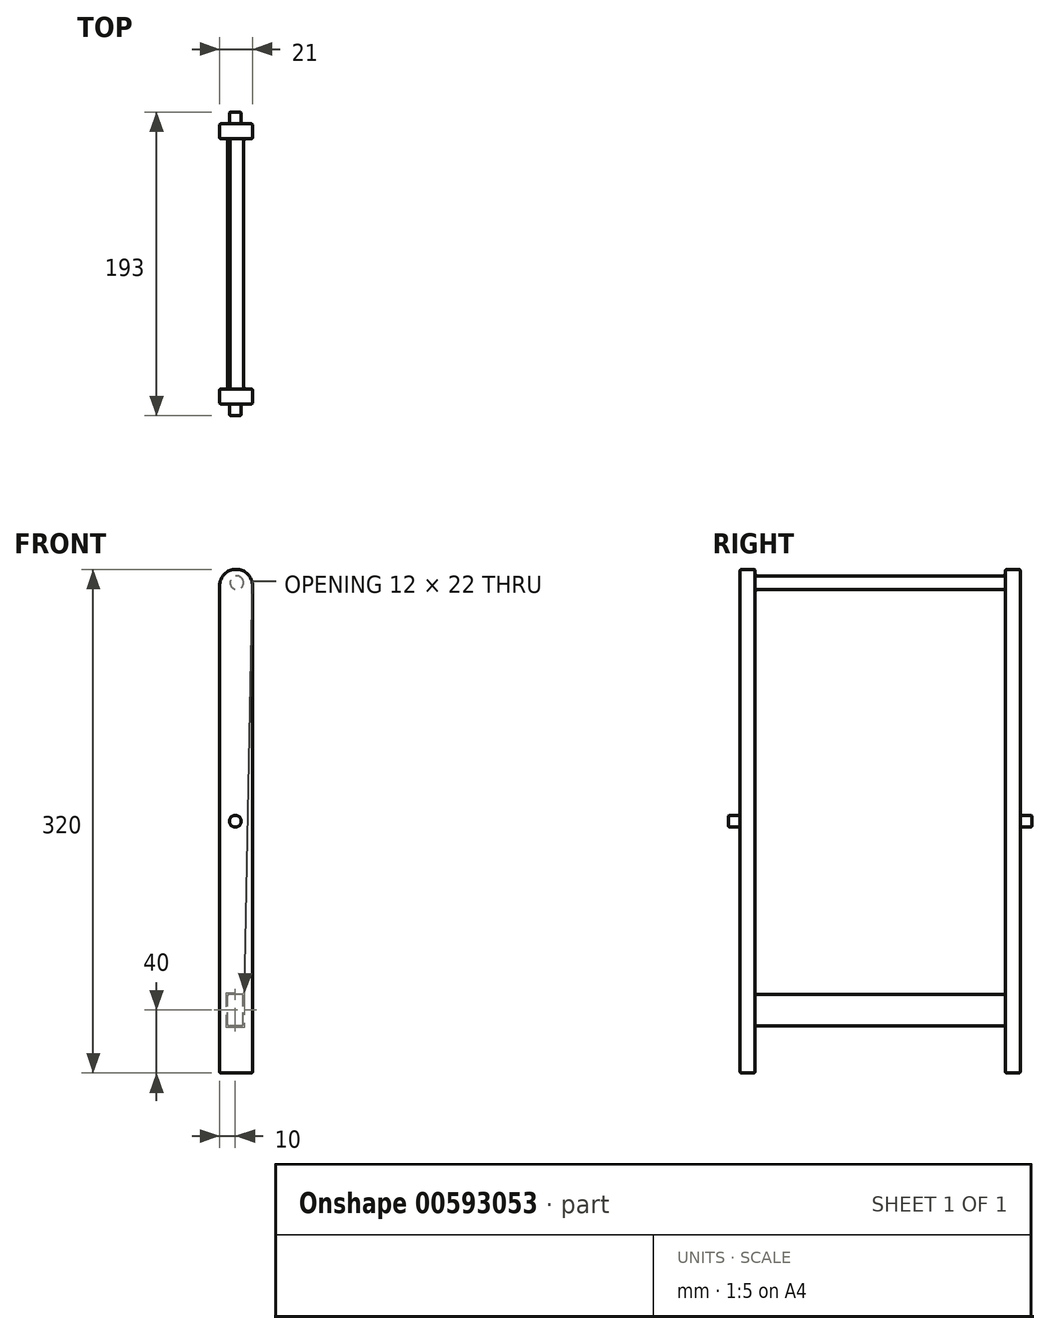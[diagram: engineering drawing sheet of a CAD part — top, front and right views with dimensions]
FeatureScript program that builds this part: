
annotation { "Feature Type Name" : "Feature", "Feature Type Description" : "" }
export const myFeature = defineFeature(function(context is Context, id is Id, definition is map)
    precondition{}
    {
        {
            var Q0;
            Q0=qCreatedBy(makeId("Front.planeOp"),FACE);
            var sketch = newSketch(context, id + "F0", { "sketchPlane" : qUnion([Q0])});
            skLineSegment(sketch, "E0.top", {"start": v(-11, -175) * mm, "end": v(10, -175) * mm});
            skLineSegment(sketch, "E0.left", {"start": v(-11, 134.5) * mm, "end": v(-11, -175) * mm});
            skLineSegment(sketch, "E0.right", {"start": v(10, 134.5) * mm, "end": v(10, -175) * mm});
            skArc(sketch, "E1", {"start": v(10, 134.5) * mm, "mid": v(-0.5, 145) * mm, "end": v(-11, 134.5) * mm});
            skSolve(sketch);
        }
        {
            var Q0;
            Q0=qSketchRegion(id+"F0",true);
            extrude(context, id + "F1", {"entities" : qUnion([Q0]), "depth" : 9.5 * mm});
        }
        {
            var Q0;
            Q0=makeQuery(id+"F1.opExtrude","CAP_FACE",FACE,{"disambiguationData":[OSD([sQuery(id+"F0.wireOp",EDGE,"E0.top"),sQuery(id+"F0.wireOp",EDGE,"E0.left"),sQuery(id+"F0.wireOp",EDGE,"E0.right"),sQuery(id+"F0.wireOp",EDGE,"E1")])],"isStart":false});
            var sketch = newSketch(context, id + "F2", { "sketchPlane" : qUnion([Q0])});
            skLineSegment(sketch, "E2.bottom", {"start": v(4, -145) * mm, "end": v(-6, -145) * mm});
            skLineSegment(sketch, "E2.top", {"start": v(4, -125) * mm, "end": v(-6, -125) * mm});
            skLineSegment(sketch, "E2.left", {"start": v(4, -145) * mm, "end": v(4, -125) * mm});
            skLineSegment(sketch, "E2.right", {"start": v(-6, -145) * mm, "end": v(-6, -125) * mm});
            skCircle(sketch, "E3", {"center": v(0, 136.5) * mm, "radius": 4.25 * mm});
            skSolve(sketch);
        }
        {
            var Q0;
            Q0=makeQuery(id+"F2.imprint","IMPRINT",FACE,{"disambiguationData":[TD([[makeQuery(id+"F2.imprint","IMPRINT",EDGE,{"derivedFrom":sQuery(id+"F2.wireOp",EDGE,"E3")}),1.0]])]});
            var Q1;
            Q1=makeQuery(id+"F2.imprint","IMPRINT",FACE,{"disambiguationData":[TD([[makeQuery(id+"F2.imprint","IMPRINT",EDGE,{"derivedFrom":sQuery(id+"F2.wireOp",EDGE,"E2.bottom")}),-1.0]])]});
            extrude(context, id + "F3", {"entities" : qUnion([Q0, Q1]), "operationType" : NewBodyOperationType.ADD, "depth" : 159 * mm});
        }
        {
            var Q0;
            Q0=makeQuery(id+"F3.opExtrude","CAP_FACE",FACE,{"disambiguationData":[OSD([sQuery(id+"F2.wireOp",EDGE,"E2.bottom"),sQuery(id+"F2.wireOp",EDGE,"E2.top"),sQuery(id+"F2.wireOp",EDGE,"E2.left"),sQuery(id+"F2.wireOp",EDGE,"E2.right")])],"isStart":false});
            var sketch = newSketch(context, id + "F4", { "sketchPlane" : qUnion([Q0])});
            skLineSegment(sketch, "E4.bottom", {"start": v(-11, -175) * mm, "end": v(10, -175) * mm});
            skLineSegment(sketch, "E4.left", {"start": v(-11, -175) * mm, "end": v(-11, 134.5) * mm});
            skLineSegment(sketch, "E4.right", {"start": v(10, -175) * mm, "end": v(10, 134.5) * mm});
            skArc(sketch, "E5", {"start": v(10, 134.5) * mm, "mid": v(-0.5, 145) * mm, "end": v(-11, 134.5) * mm});
            skSolve(sketch);
        }
        {
            var Q0;
            Q0=makeQuery(id+"F4.imprint","IMPRINT",FACE,{"disambiguationData":[TD([[makeQuery(id+"F4.imprint","IMPRINT",EDGE,{"derivedFrom":sQuery(id+"F4.wireOp",EDGE,"E4.bottom")}),1.0]])]});
            var Q1;
            Q1=makeQuery(id+"F4.imprint","IMPRINT",FACE,{"disambiguationData":[TD([[makeQuery(id+"F4.imprint","IMPRINT",EDGE,{"derivedFrom":makeQuery(id+"F3.opExtrude","CAP_EDGE",EDGE,{"disambiguationData":[OSD([sQuery(id+"F2.wireOp",EDGE,"E2.bottom")])],"isStart":false})}),-1.0]])]});
            extrude(context, id + "F5", {"entities" : qUnion([Q0, Q1]), "operationType" : NewBodyOperationType.ADD, "depth" : 9.5 * mm});
        }
        {
            var Q0;
            Q0=makeQuery(id+"F5.opExtrude","CAP_FACE",FACE,{"disambiguationData":[OSD([sQuery(id+"F4.wireOp",EDGE,"E4.bottom"),sQuery(id+"F4.wireOp",EDGE,"E4.left"),sQuery(id+"F4.wireOp",EDGE,"E4.right"),sQuery(id+"F4.wireOp",EDGE,"E5")])],"isStart":false});
            var sketch = newSketch(context, id + "F6", { "sketchPlane" : qUnion([Q0])});
            skCircle(sketch, "E6", {"center": v(-1, -15) * mm, "radius": 3.75 * mm});
            skSolve(sketch);
        }
        {
            var Q0;
            Q0=makeQuery(id+"F0.imprint","IMPRINT",FACE,{"disambiguationData":[TD([[makeQuery(id+"F0.imprint","IMPRINT",EDGE,{"derivedFrom":sQuery(id+"F0.wireOp",EDGE,"E0.top")}),1.0]])]});
            var sketch = newSketch(context, id + "F7", { "sketchPlane" : qUnion([Q0])});
            skCircle(sketch, "E7", {"center": v(-1, -15) * mm, "radius": 3.75 * mm});
            skSolve(sketch);
        }
        {
            var Q0;
            Q0=qSketchRegion(id+"F6",true);
            var Q1;
            Q1=qSketchRegion(id+"F7",true);
            extrude(context, id + "F8", {"entities" : qUnion([Q0, Q1]), "operationType" : NewBodyOperationType.ADD, "depth" : 15 * mm, "symmetric" : true});
        }
        {
            var Q0;
            Q0=makeQuery(id+"F8.opExtrude","SWEPT_FACE",FACE,{"disambiguationData":[OSD([sQuery(id+"F7.wireOp",EDGE,"E7")])]});
            var Q1;
            Q1=makeQuery(id+"F8.opExtrude","SWEPT_FACE",FACE,{"disambiguationData":[OSD([sQuery(id+"F6.wireOp",EDGE,"E6")])]});
            fillet(context, id + "F9", {"entities" : qUnion([Q0, Q1]), "radius" : 1 * mm, "tangentPropagation" : true, "allowEdgeOverflow" : false});
        }
        {
            var Q0;
            Q0=makeQuery(id+"F3.opExtrude","CAP_EDGE",EDGE,{"disambiguationData":[OSD([sQuery(id+"F2.wireOp",EDGE,"E2.right")])],"isStart":true});
            var Q1;
            Q1=makeQuery(id+"F3.opExtrude","CAP_EDGE",EDGE,{"disambiguationData":[OSD([sQuery(id+"F2.wireOp",EDGE,"E2.left")])],"isStart":true});
            var Q2;
            Q2=makeQuery(id+"F3.opExtrude","CAP_EDGE",EDGE,{"disambiguationData":[OSD([sQuery(id+"F2.wireOp",EDGE,"E2.bottom")])],"isStart":true});
            var Q3;
            Q3=makeQuery(id+"F3.opExtrude","CAP_EDGE",EDGE,{"disambiguationData":[OSD([sQuery(id+"F2.wireOp",EDGE,"E2.top")])],"isStart":true});
            var Q4;
            Q4=makeQuery(id+"F3.opExtrude","CAP_EDGE",EDGE,{"disambiguationData":[OSD([sQuery(id+"F2.wireOp",EDGE,"E2.top")])],"isStart":false});
            var Q5;
            Q5=makeQuery(id+"F3.opExtrude","CAP_EDGE",EDGE,{"disambiguationData":[OSD([sQuery(id+"F2.wireOp",EDGE,"E2.right")])],"isStart":false});
            var Q6;
            Q6=makeQuery(id+"F3.opExtrude","SWEPT_FACE",FACE,{"disambiguationData":[OSD([sQuery(id+"F2.wireOp",EDGE,"E3")])]});
            var Q7;
            Q7=makeQuery(id+"F3.opExtrude","CAP_EDGE",EDGE,{"disambiguationData":[OSD([sQuery(id+"F2.wireOp",EDGE,"E2.left")])],"isStart":false});
            var Q8;
            Q8=makeQuery(id+"F3.opExtrude","CAP_EDGE",EDGE,{"disambiguationData":[OSD([sQuery(id+"F2.wireOp",EDGE,"E2.bottom")])],"isStart":false});
            fillet(context, id + "F10", {"entities" : qUnion([Q0, Q1, Q2, Q3, Q4, Q5, Q6, Q7, Q8]), "radius" : 2 * mm, "tangentPropagation" : true, "allowEdgeOverflow" : false});
        }
        {
            var Q0;
            Q0=makeQuery(id+"F1.opExtrude","SWEPT_FACE",FACE,{"disambiguationData":[OSD([sQuery(id+"F0.wireOp",EDGE,"E0.top")])]});
            var Q1;
            Q1=makeQuery(id+"F5.opExtrude","SWEPT_FACE",FACE,{"disambiguationData":[OSD([sQuery(id+"F4.wireOp",EDGE,"E4.bottom")])]});
            var Q2;
            Q2=makeQuery(id+"F1.opExtrude","CAP_FACE",FACE,{"disambiguationData":[OSD([sQuery(id+"F0.wireOp",EDGE,"E0.top"),sQuery(id+"F0.wireOp",EDGE,"E0.left"),sQuery(id+"F0.wireOp",EDGE,"E0.right"),sQuery(id+"F0.wireOp",EDGE,"E1")])],"isStart":true});
            var Q3;
            Q3=makeQuery(id+"F5.opExtrude","CAP_FACE",FACE,{"disambiguationData":[OSD([sQuery(id+"F4.wireOp",EDGE,"E4.bottom"),sQuery(id+"F4.wireOp",EDGE,"E4.left"),sQuery(id+"F4.wireOp",EDGE,"E4.right"),sQuery(id+"F4.wireOp",EDGE,"E5")])],"isStart":false});
            var Q4;
            Q4=makeQuery(id+"F5.opExtrude","SWEPT_FACE",FACE,{"disambiguationData":[OSD([sQuery(id+"F4.wireOp",EDGE,"E4.left")])]});
            var Q5;
            Q5=makeQuery(id+"F1.opExtrude","SWEPT_FACE",FACE,{"disambiguationData":[OSD([sQuery(id+"F0.wireOp",EDGE,"E0.left")])]});
            var Q6;
            Q6=makeQuery(id+"F3.opExtrude","SWEPT_FACE",FACE,{"disambiguationData":[OSD([sQuery(id+"F2.wireOp",EDGE,"E2.right")])]});
            var Q7;
            Q7=makeQuery(id+"F3.opExtrude","SWEPT_FACE",FACE,{"disambiguationData":[OSD([sQuery(id+"F2.wireOp",EDGE,"E2.bottom")])]});
            var Q8;
            Q8=makeQuery(id+"F3.opExtrude","SWEPT_FACE",FACE,{"disambiguationData":[OSD([sQuery(id+"F2.wireOp",EDGE,"E2.left")])]});
            var Q9;
            Q9=makeQuery(id+"F3.opExtrude","SWEPT_FACE",FACE,{"disambiguationData":[OSD([sQuery(id+"F2.wireOp",EDGE,"E2.top")])]});
            fillet(context, id + "F11", {"entities" : qUnion([Q0, Q1, Q2, Q3, Q4, Q5, Q6, Q7, Q8, Q9]), "radius" : 1 * mm, "tangentPropagation" : true, "allowEdgeOverflow" : false});
        }
    });
